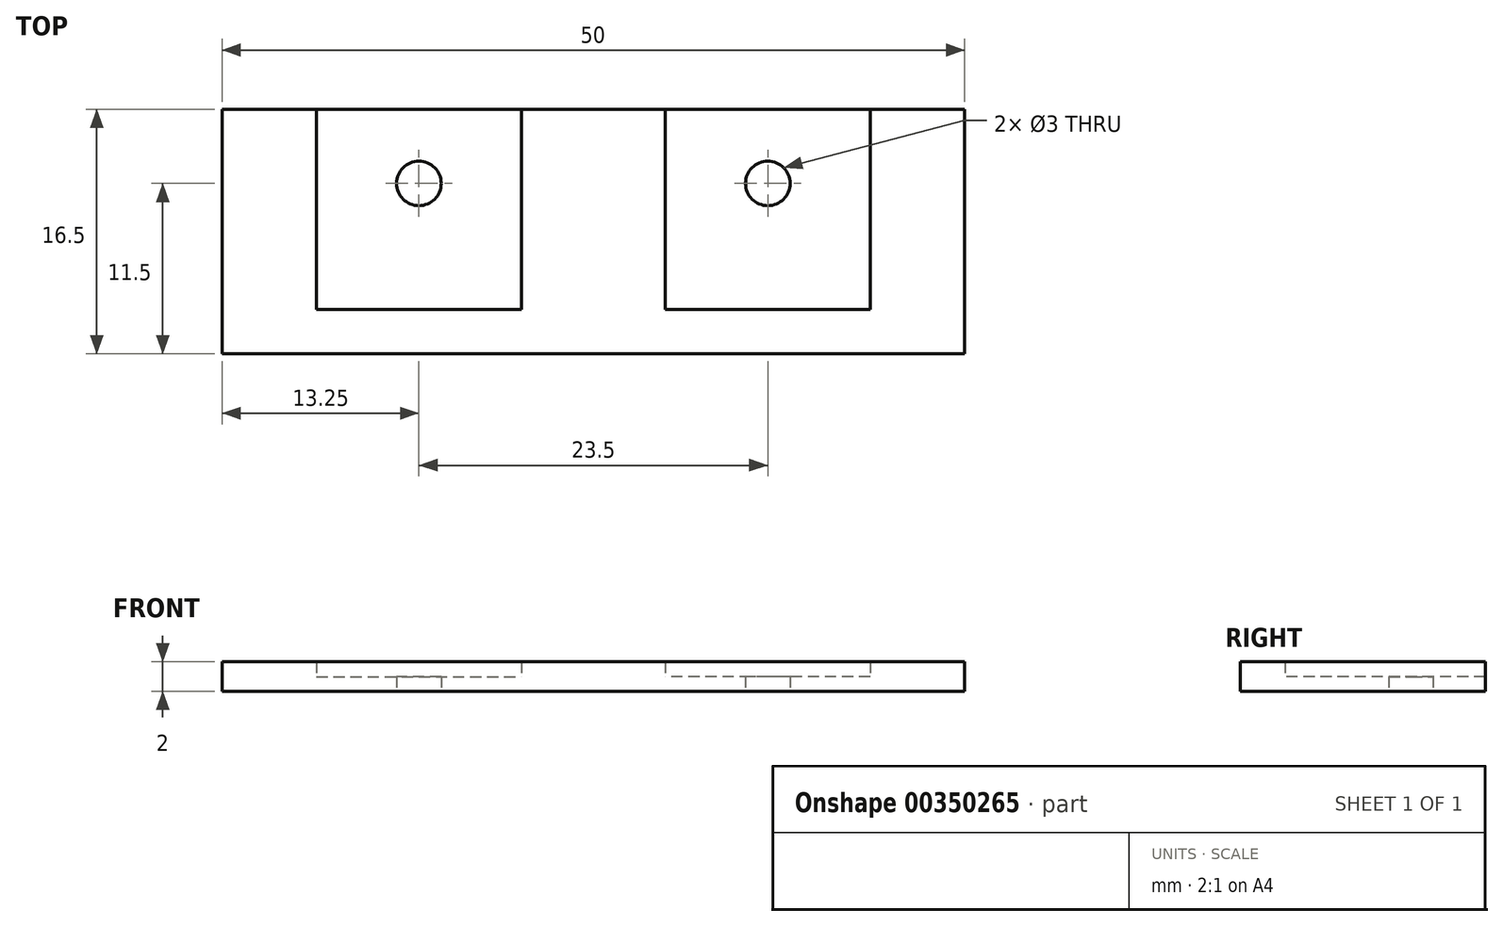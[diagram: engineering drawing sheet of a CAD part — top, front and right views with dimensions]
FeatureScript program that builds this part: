
annotation { "Feature Type Name" : "Feature", "Feature Type Description" : "" }
export const myFeature = defineFeature(function(context is Context, id is Id, definition is map)
    precondition{}
    {
        {
            var Q0;
            Q0=qCreatedBy(makeId("Top.planeOp"),FACE);
            var sketch = newSketch(context, id + "F0", { "sketchPlane" : qUnion([Q0])});
            skCircle(sketch, "E0", {"center": v(-11.75, 0) * mm, "radius": 1.5 * mm});
            skLineSegment(sketch, "E1", {"start": v(-18.65, 5) * mm, "end": v(-18.65, -8.5) * mm});
            skLineSegment(sketch, "E2", {"start": v(-18.65, -8.5) * mm, "end": v(-4.85, -8.5) * mm});
            skLineSegment(sketch, "E3", {"start": v(-4.85, -8.5) * mm, "end": v(-4.85, 5) * mm});
            skLineSegment(sketch, "E4.bottom", {"start": v(-25, 5) * mm, "end": v(0, 5) * mm});
            skLineSegment(sketch, "E4.top", {"start": v(-25, -11.5) * mm, "end": v(0, -11.5) * mm});
            skLineSegment(sketch, "E4.left", {"start": v(-25, 5) * mm, "end": v(-25, -11.5) * mm});
            skPoint(sketch, "E5.center.orphan", {"position": v(11.75, 0) * mm});
            skLineSegment(sketch, "E6.MirrorCS", {"start": v(4.85, -8.5) * mm, "end": v(4.85, 5) * mm});
            skLineSegment(sketch, "E7.MirrorCS", {"start": v(25, 5) * mm, "end": v(0, 5) * mm});
            skLineSegment(sketch, "E8.MirrorCS", {"start": v(25, -11.5) * mm, "end": v(0, -11.5) * mm});
            skLineSegment(sketch, "E9.MirrorCS", {"start": v(18.65, -8.5) * mm, "end": v(4.85, -8.5) * mm});
            skCircle(sketch, "E10.MirrorC", {"center": v(11.75, 0) * mm, "radius": 1.5 * mm});
            skLineSegment(sketch, "E11.MirrorCS", {"start": v(25, 5) * mm, "end": v(25, -11.5) * mm});
            skLineSegment(sketch, "E12.MirrorCS", {"start": v(18.65, 5) * mm, "end": v(18.65, -8.5) * mm});
            skSolve(sketch);
        }
        {
            var Q0;
            {var subQ8=sQuery(id+"F0.wireOp",EDGE,"E1");Q0=makeQuery(id+"F0.imprint","IMPRINT",FACE,{"disambiguationData":[TD([[makeQuery(id+"F0.imprint","IMPRINT",EDGE,{"derivedFrom":subQ8}),-1.0]])]});}
            extrude(context, id + "F1", {"entities" : qUnion([Q0]), "depth" : 2 * mm});
        }
        {
            var Q0;
            Q0 = qSketchRegion(id + "F0", true);
            extrude(context, id + "F2", {"entities" : qUnion([Q0]), "operationType" : NewBodyOperationType.ADD, "depth" : 1 * mm});
        }
    });
